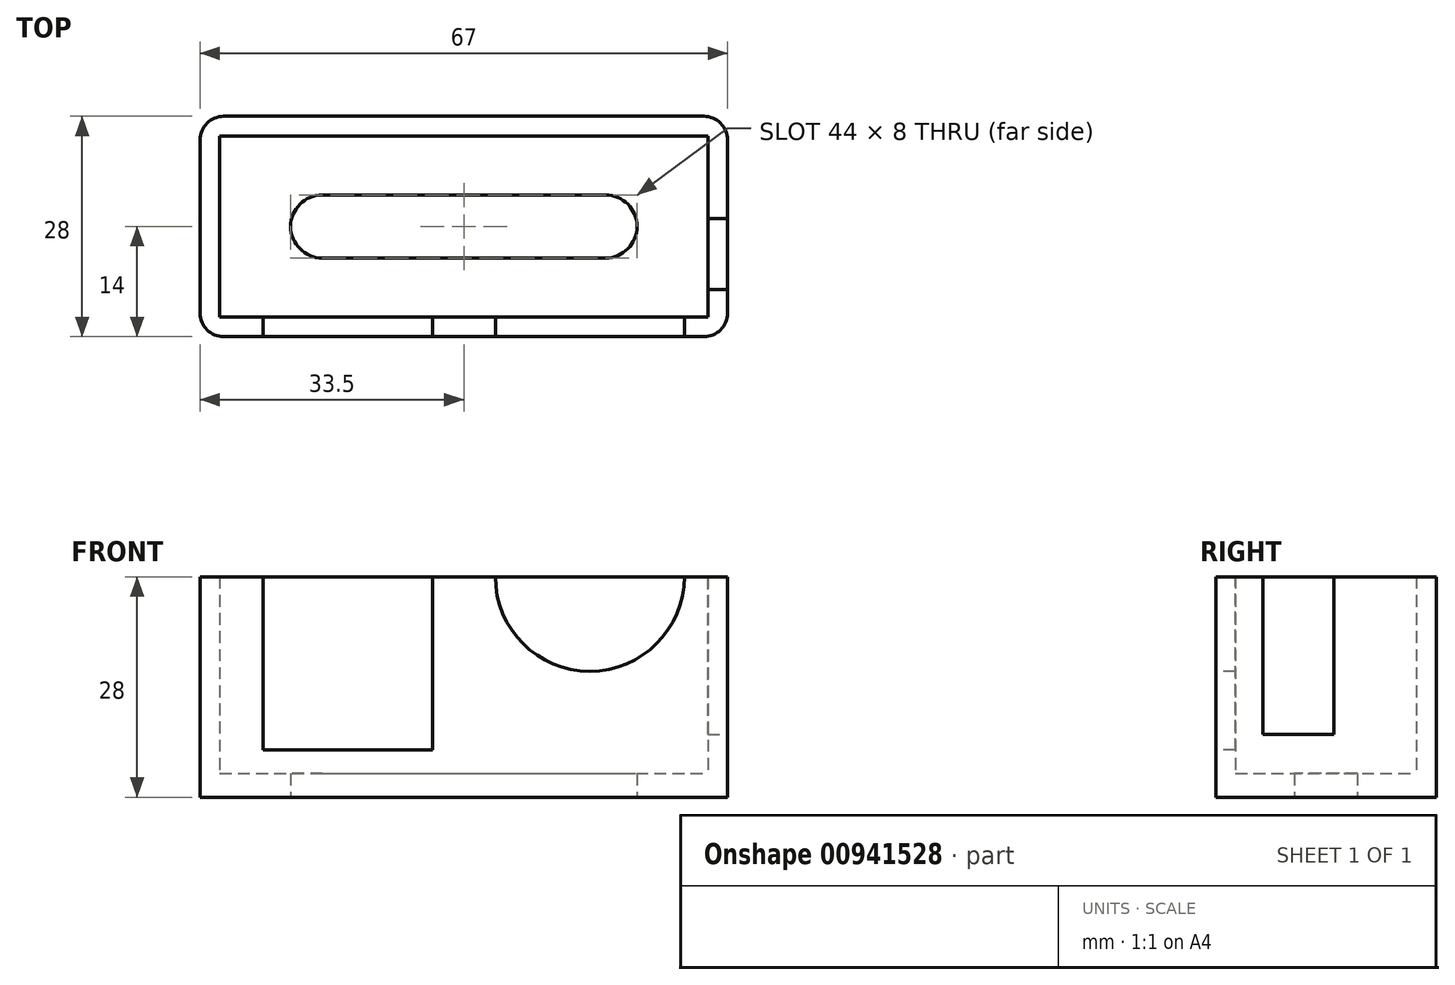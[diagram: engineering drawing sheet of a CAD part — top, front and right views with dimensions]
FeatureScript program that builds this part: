
annotation { "Feature Type Name" : "Feature", "Feature Type Description" : "" }
export const myFeature = defineFeature(function(context is Context, id is Id, definition is map)
    precondition{}
    {
        {
            var Q0;
            Q0=qCreatedBy(makeId("Top.planeOp"),FACE);
            var sketch = newSketch(context, id + "F0", { "sketchPlane" : qUnion([Q0])});
            skLineSegment(sketch, "E0.bottom", {"start": v(0, 0) * mm, "end": v(62, 0) * mm});
            skLineSegment(sketch, "E0.top", {"start": v(0, 23) * mm, "end": v(62, 23) * mm});
            skLineSegment(sketch, "E0.left", {"start": v(0, 0) * mm, "end": v(0, 23) * mm});
            skLineSegment(sketch, "E0.right", {"start": v(62, 0) * mm, "end": v(62, 23) * mm});
            skLineSegment(sketch, "E1.bottom", {"start": v(62, 0) * mm, "end": v(64.5, 0) * mm});
            skLineSegment(sketch, "E1.top", {"start": v(62, 25.5) * mm, "end": v(64.5, 25.5) * mm});
            skLineSegment(sketch, "E1.left", {"start": v(62, 0) * mm, "end": v(62, 25.5) * mm});
            skLineSegment(sketch, "E1.right", {"start": v(64.5, 0) * mm, "end": v(64.5, 25.5) * mm});
            skLineSegment(sketch, "E2.left", {"start": v(62, 23) * mm, "end": v(62, 25.5) * mm});
            skLineSegment(sketch, "E3.bottom", {"start": v(62, 23) * mm, "end": v(-2.5, 23) * mm});
            skLineSegment(sketch, "E3.top", {"start": v(62, 25.5) * mm, "end": v(-2.5, 25.5) * mm});
            skLineSegment(sketch, "E3.right", {"start": v(-2.5, 23) * mm, "end": v(-2.5, 25.5) * mm});
            skLineSegment(sketch, "E4.bottom", {"start": v(0, 23) * mm, "end": v(-2.5, 23) * mm});
            skLineSegment(sketch, "E4.top", {"start": v(0, -2.5) * mm, "end": v(-2.5, -2.5) * mm});
            skLineSegment(sketch, "E4.left", {"start": v(0, 23) * mm, "end": v(0, -2.5) * mm});
            skLineSegment(sketch, "E4.right", {"start": v(-2.5, 23) * mm, "end": v(-2.5, -2.5) * mm});
            skLineSegment(sketch, "E5.bottom", {"start": v(0, 0) * mm, "end": v(64.5, 0) * mm});
            skLineSegment(sketch, "E5.top", {"start": v(0, -2.5) * mm, "end": v(64.5, -2.5) * mm});
            skLineSegment(sketch, "E5.left", {"start": v(0, 0) * mm, "end": v(0, -2.5) * mm});
            skLineSegment(sketch, "E5.right", {"start": v(64.5, 0) * mm, "end": v(64.5, -2.5) * mm});
            skSolve(sketch);
        }
        {
            var Q0;
            Q0=makeQuery(id+"F0.imprint","IMPRINT",FACE,{"disambiguationData":[TD([[makeQuery(id+"F0.imprint","IMPRINT",EDGE,{"derivedFrom":sQuery(id+"F0.wireOp",EDGE,"E0.top")}),1.0]])]});
            var Q1;
            Q1=makeQuery(id+"F0.imprint","IMPRINT",FACE,{"disambiguationData":[TD([[makeQuery(id+"F0.imprint","IMPRINT",EDGE,{"derivedFrom":sQuery(id+"F0.wireOp",EDGE,"E0.left")}),1.0]])]});
            var Q2;
            Q2=makeQuery(id+"F0.imprint","IMPRINT",FACE,{"disambiguationData":[TD([[makeQuery(id+"F0.imprint","IMPRINT",EDGE,{"derivedFrom":sQuery(id+"F0.wireOp",EDGE,"E0.bottom")}),-1.0]])]});
            var Q3;
            Q3=makeQuery(id+"F0.imprint","IMPRINT",FACE,{"disambiguationData":[TD([[makeQuery(id+"F0.imprint","IMPRINT",EDGE,{"derivedFrom":sQuery(id+"F0.wireOp",EDGE,"E0.right")}),-1.0]])]});
            extrude(context, id + "F1", {"entities" : qUnion([Q0, Q1, Q2, Q3]), "depth" : 25 * mm, "offsetDistance" : 25 * mm});
        }
        {
            var Q0;
            Q0=makeQuery(id+"F0.imprint","IMPRINT",FACE,{"disambiguationData":[TD([[makeQuery(id+"F0.imprint","IMPRINT",EDGE,{"derivedFrom":sQuery(id+"F0.wireOp",EDGE,"E0.right")}),-1.0]])]});
            var Q1;
            Q1=makeQuery(id+"F0.imprint","IMPRINT",FACE,{"disambiguationData":[TD([[makeQuery(id+"F0.imprint","IMPRINT",EDGE,{"derivedFrom":sQuery(id+"F0.wireOp",EDGE,"E0.bottom")}),1.0]])]});
            var Q2;
            Q2=makeQuery(id+"F0.imprint","IMPRINT",FACE,{"disambiguationData":[TD([[makeQuery(id+"F0.imprint","IMPRINT",EDGE,{"derivedFrom":sQuery(id+"F0.wireOp",EDGE,"E0.bottom")}),-1.0]])]});
            var Q3;
            Q3=makeQuery(id+"F0.imprint","IMPRINT",FACE,{"disambiguationData":[TD([[makeQuery(id+"F0.imprint","IMPRINT",EDGE,{"derivedFrom":sQuery(id+"F0.wireOp",EDGE,"E0.left")}),1.0]])]});
            var Q4;
            Q4=makeQuery(id+"F0.imprint","IMPRINT",FACE,{"disambiguationData":[TD([[makeQuery(id+"F0.imprint","IMPRINT",EDGE,{"derivedFrom":sQuery(id+"F0.wireOp",EDGE,"E0.top")}),1.0]])]});
            extrude(context, id + "F2", {"entities" : qUnion([Q0, Q1, Q2, Q3, Q4]), "operationType" : NewBodyOperationType.ADD, "oppositeDirection" : true, "depth" : 3 * mm, "offsetDistance" : 25 * mm});
        }
        {
            var Q0;
            Q0=makeQuery(id+"F2.opExtrude","CAP_FACE",FACE,{"disambiguationData":[OSD([sQuery(id+"F0.wireOp",EDGE,"E1.top"),sQuery(id+"F0.wireOp",EDGE,"E1.right"),sQuery(id+"F0.wireOp",EDGE,"E3.top"),sQuery(id+"F0.wireOp",EDGE,"E3.right"),sQuery(id+"F0.wireOp",EDGE,"E4.top"),sQuery(id+"F0.wireOp",EDGE,"E4.right"),sQuery(id+"F0.wireOp",EDGE,"E5.top"),sQuery(id+"F0.wireOp",EDGE,"E5.right")])],"isStart":false});
            var sketch = newSketch(context, id + "F3", { "sketchPlane" : qUnion([Q0])});
            skLineSegment(sketch, "E6", {"start": v(31, -7.5) * mm, "end": v(13, -7.5) * mm});
            skLineSegment(sketch, "E7", {"start": v(31, -7.5) * mm, "end": v(49, -7.5) * mm});
            skLineSegment(sketch, "E8", {"start": v(31, -15.5) * mm, "end": v(49, -15.5) * mm});
            skLineSegment(sketch, "E9", {"start": v(31, -15.5) * mm, "end": v(13, -15.5) * mm});
            skArc(sketch, "E10", {"start": v(13, -7.5) * mm, "mid": v(9, -11.5) * mm, "end": v(13, -15.5) * mm});
            skArc(sketch, "E11", {"start": v(49, -15.5) * mm, "mid": v(53, -11.5) * mm, "end": v(49, -7.5) * mm});
            skSolve(sketch);
        }
        {
            var Q0;
            Q0 = qSketchRegion(id + "F3", true);
            extrude(context, id + "F4", {"entities" : qUnion([Q0]), "operationType" : NewBodyOperationType.REMOVE, "oppositeDirection" : true, "depth" : 25 * mm, "offsetDistance" : 25 * mm});
        }
        {
            var Q0;
            {var subQ0=sQuery(id+"F0.wireOp",EDGE,"E5.top");var subQ1=sQuery(id+"F0.wireOp",EDGE,"E4.top");Q0=makeQuery(id+"F2.boolean.opBoolean","MERGE",FACE,{"derivedFrom":[makeQuery(id+"F1.opExtrude","SWEPT_FACE",FACE,{"disambiguationData":[OSD([subQ1,subQ0])]}),makeQuery(id+"F2.opExtrude","SWEPT_FACE",FACE,{"disambiguationData":[OSD([subQ1,subQ0])]})]});}
            var sketch = newSketch(context, id + "F5", { "sketchPlane" : qUnion([Q0])});
            skLineSegment(sketch, "E12", {"start": v(5.5, 25) * mm, "end": v(5.5, 3) * mm});
            skLineSegment(sketch, "E13", {"start": v(64.5, 25) * mm, "end": v(64.5, 0) * mm});
            skLineSegment(sketch, "E14", {"start": v(5.5, 3) * mm, "end": v(27, 3) * mm});
            skLineSegment(sketch, "E15", {"start": v(27, 3) * mm, "end": v(27, 25) * mm});
            skArc(sketch, "E16", {"start": v(35, 25) * mm, "mid": v(47, 13) * mm, "end": v(59, 25) * mm});
            skSolve(sketch);
        }
        {
            var Q0;
            {var subQ0=sQuery(id+"F5.wireOp",EDGE,"E12");Q0=makeQuery(id+"F5.imprint","IMPRINT",FACE,{"disambiguationData":[TD([[makeQuery(id+"F5.imprint","IMPRINT",EDGE,{"derivedFrom":subQ0}),1.0]])]});}
            var Q1;
            {var subQ0=sQuery(id+"F5.wireOp",EDGE,"E16");Q1=makeQuery(id+"F5.imprint","IMPRINT",FACE,{"disambiguationData":[TD([[makeQuery(id+"F5.imprint","IMPRINT",EDGE,{"derivedFrom":subQ0}),1.0]])]});}
            extrude(context, id + "F6", {"entities" : qUnion([Q0, Q1]), "operationType" : NewBodyOperationType.REMOVE, "oppositeDirection" : true, "depth" : 3 * mm, "offsetDistance" : 25 * mm});
        }
        {
            var Q0;
            {var subQ0=sQuery(id+"F0.wireOp",EDGE,"E5.right");var subQ1=sQuery(id+"F0.wireOp",EDGE,"E1.right");Q0=makeQuery(id+"F2.boolean.opBoolean","MERGE",FACE,{"derivedFrom":[makeQuery(id+"F1.opExtrude","SWEPT_FACE",FACE,{"disambiguationData":[OSD([subQ1,subQ0])]}),makeQuery(id+"F2.opExtrude","SWEPT_FACE",FACE,{"disambiguationData":[OSD([subQ1,subQ0])]})]});}
            var sketch = newSketch(context, id + "F7", { "sketchPlane" : qUnion([Q0])});
            skLineSegment(sketch, "E17", {"start": v(3.5, 25) * mm, "end": v(12.5, 25) * mm});
            skLineSegment(sketch, "E18", {"start": v(12.5, 25) * mm, "end": v(12.5, 5) * mm});
            skLineSegment(sketch, "E19", {"start": v(12.5, 5) * mm, "end": v(3.5, 5) * mm});
            skLineSegment(sketch, "E20", {"start": v(3.5, 5) * mm, "end": v(3.5, 25) * mm});
            skSolve(sketch);
        }
        {
            var Q0;
            Q0 = qSketchRegion(id + "F7", true);
            extrude(context, id + "F8", {"entities" : qUnion([Q0]), "operationType" : NewBodyOperationType.REMOVE, "oppositeDirection" : true, "depth" : 5 * mm, "offsetDistance" : 25 * mm});
        }
        {
            var Q0;
            {var subQ0=sQuery(id+"F0.wireOp",EDGE,"E5.right");var subQ1=sQuery(id+"F0.wireOp",EDGE,"E5.top");Q0=makeQuery(id+"F2.boolean.opBoolean","MERGE",EDGE,{"derivedFrom":[makeQuery(id+"F1.opExtrude","SWEPT_EDGE",EDGE,{"disambiguationData":[OSD([subQ1,subQ0])]}),makeQuery(id+"F2.opExtrude","SWEPT_EDGE",EDGE,{"disambiguationData":[OSD([subQ1,subQ0])]})]});}
            var Q1;
            {var subQ0=sQuery(id+"F0.wireOp",EDGE,"E1.right");var subQ1=sQuery(id+"F0.wireOp",EDGE,"E1.top");Q1=makeQuery(id+"F2.boolean.opBoolean","MERGE",EDGE,{"derivedFrom":[makeQuery(id+"F1.opExtrude","SWEPT_EDGE",EDGE,{"disambiguationData":[OSD([subQ1,subQ0])]}),makeQuery(id+"F2.opExtrude","SWEPT_EDGE",EDGE,{"disambiguationData":[OSD([subQ1,subQ0])]})]});}
            var Q2;
            {var subQ0=sQuery(id+"F0.wireOp",EDGE,"E3.right");var subQ1=sQuery(id+"F0.wireOp",EDGE,"E3.top");Q2=makeQuery(id+"F2.boolean.opBoolean","MERGE",EDGE,{"derivedFrom":[makeQuery(id+"F1.opExtrude","SWEPT_EDGE",EDGE,{"disambiguationData":[OSD([subQ1,subQ0])]}),makeQuery(id+"F2.opExtrude","SWEPT_EDGE",EDGE,{"disambiguationData":[OSD([subQ1,subQ0])]})]});}
            var Q3;
            {var subQ0=sQuery(id+"F0.wireOp",EDGE,"E4.right");var subQ1=sQuery(id+"F0.wireOp",EDGE,"E4.top");Q3=makeQuery(id+"F2.boolean.opBoolean","MERGE",EDGE,{"derivedFrom":[makeQuery(id+"F1.opExtrude","SWEPT_EDGE",EDGE,{"disambiguationData":[OSD([subQ1,subQ0])]}),makeQuery(id+"F2.opExtrude","SWEPT_EDGE",EDGE,{"disambiguationData":[OSD([subQ1,subQ0])]})]});}
            fillet(context, id + "F9", {"entities" : qUnion([Q0, Q1, Q2, Q3]), "radius" : 3 * mm, "tangentPropagation" : true, "allowEdgeOverflow" : false});
        }
    });
